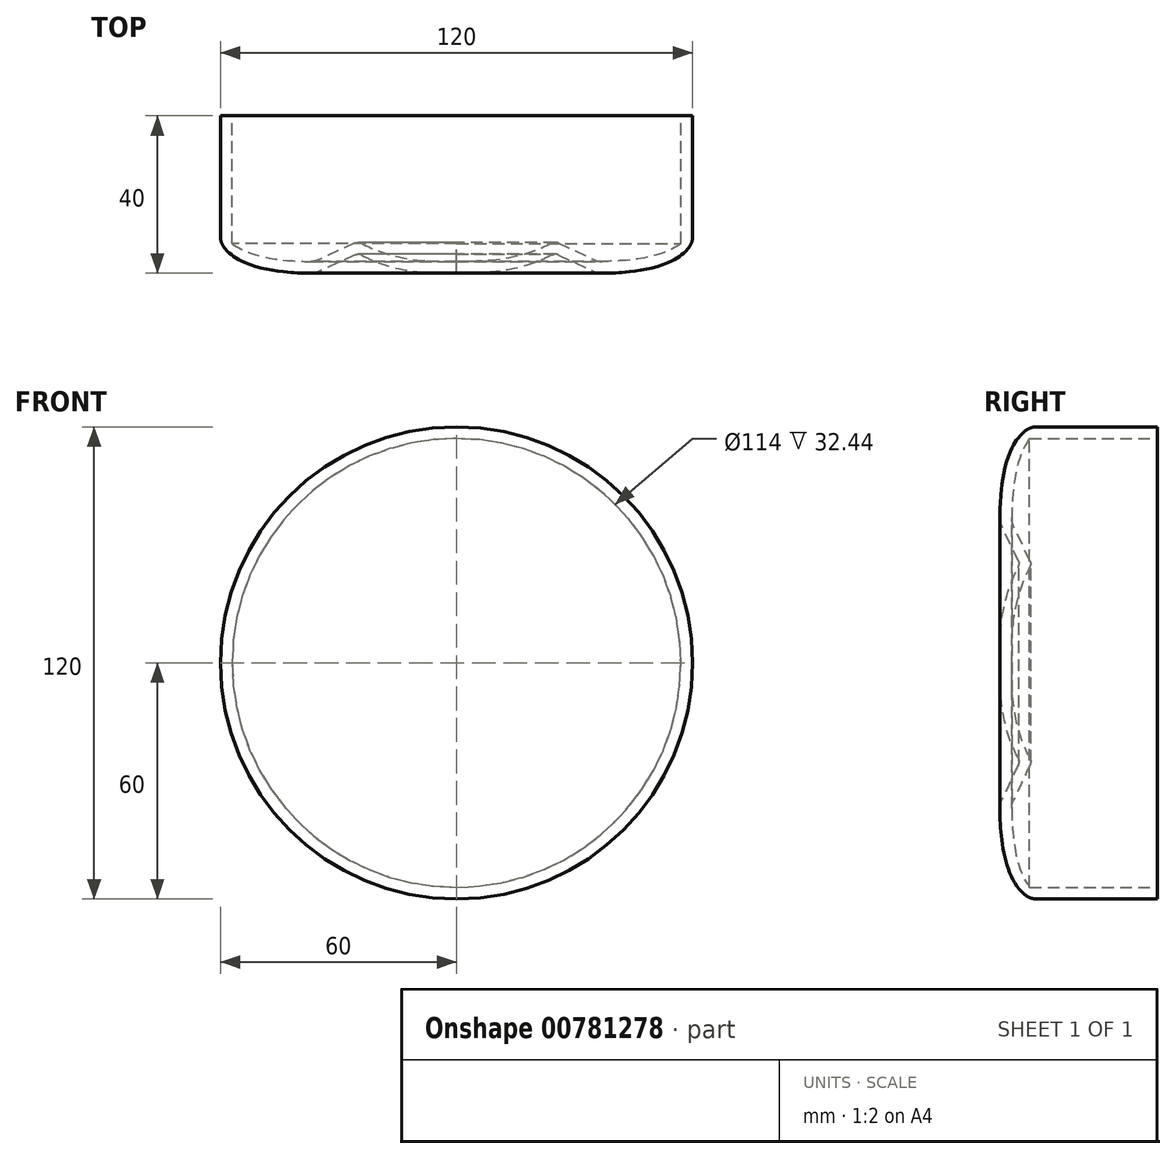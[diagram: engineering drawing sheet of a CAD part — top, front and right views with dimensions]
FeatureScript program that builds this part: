
annotation { "Feature Type Name" : "Feature", "Feature Type Description" : "" }
export const myFeature = defineFeature(function(context is Context, id is Id, definition is map)
    precondition{}
    {
        {
            var Q0;
            Q0=qCreatedBy(makeId("Right.planeOp"),FACE);
            var sketch = newSketch(context, id + "F0", { "sketchPlane" : qUnion([Q0])});
            skLineSegment(sketch, "E0", {"start": v(-54.2, 0) * mm, "end": v(63.86, 0) * mm, "construction": true});
            skFitSpline(sketch, "E1", {"points": [v(0, 0) * mm, v(5.09, 25) * mm], "startDerivative": vector(0, 21.77) * mm, "endDerivative": vector(15.26, 27.44) * mm});
            skLineSegment(sketch, "E2", {"start": v(4.66, 25.91) * mm, "end": v(0.48, 34.83) * mm});
            skFitSpline(sketch, "E3", {"points": [v(0, 35.85) * mm, v(8, 60) * mm], "startDerivative": vector(0, 22.27) * mm, "endDerivative": vector(22.14, 11.78) * mm});
            skLineSegment(sketch, "E4", {"start": v(9.5, 60) * mm, "end": v(40, 60) * mm});
            skLineSegment(sketch, "E5", {"start": v(40, 60) * mm, "end": v(40, 0) * mm});
            skArc(sketch, "E6.filletArc", {"start": v(9.5, 60) * mm, "mid": v(7.76, 59.7) * mm, "end": v(6.25, 58.8) * mm});
            skArc(sketch, "E7.filletArc", {"start": v(0, 37) * mm, "mid": v(0.12, 35.89) * mm, "end": v(0.48, 34.83) * mm});
            skArc(sketch, "E8.filletArc", {"start": v(4.62, 24.14) * mm, "mid": v(4.85, 25.02) * mm, "end": v(4.66, 25.91) * mm});
            skLineSegment(sketch, "E9", {"start": v(40, 0) * mm, "end": v(0, 0) * mm});
            skSolve(sketch);
        }
        {
            var Q0;
            Q0 = qSketchRegion(id + "F0", true);
            var Q1;
            Q1 = qConstructionFilter(qBodyType(qCreatedBy(id + "F0" ,EDGE), BodyType.WIRE), ConstructionObject.NO);
            var Q2;
            Q2=sQuery(id+"F0.wireOp",EDGE,"E0");
            revolve(context, id + "F1", {"surfaceOperationType" : NewSurfaceOperationType.NEW, "entities" : qUnion([Q0]), "surfaceEntities" : qUnion([Q1]), "axis" : qUnion([Q2]), "revolveType" : RevolveType.FULL});
        }
        {
            var Q0;
            Q0=makeQuery(id+"F1.opRevolve","SWEPT_FACE",FACE,{"disambiguationData":[OSD([sQuery(id+"F0.wireOp",EDGE,"E5")])]});
            var sketch = newSketch(context, id + "F2", { "sketchPlane" : qUnion([Q0])});
            skCircle(sketch, "E10", {"center": v(0, 0) * mm, "radius": 57 * mm});
            skSolve(sketch);
        }
        {
            var Q0;
            Q0=makeQuery(id+"F2.imprint","IMPRINT",FACE,{"disambiguationData":[TD([[makeQuery(id+"F2.imprint","IMPRINT",EDGE,{"derivedFrom":sQuery(id+"F2.wireOp",EDGE,"E10")}),1.0]])]});
            extrude(context, id + "F3", {"entities" : qUnion([Q0]), "operationType" : NewBodyOperationType.REMOVE, "endBound" : BoundingType.UP_TO_NEXT, "oppositeDirection" : true, "depth" : 25 * mm, "hasOffset" : true, "offsetDistance" : 3 * mm});
        }
    });
